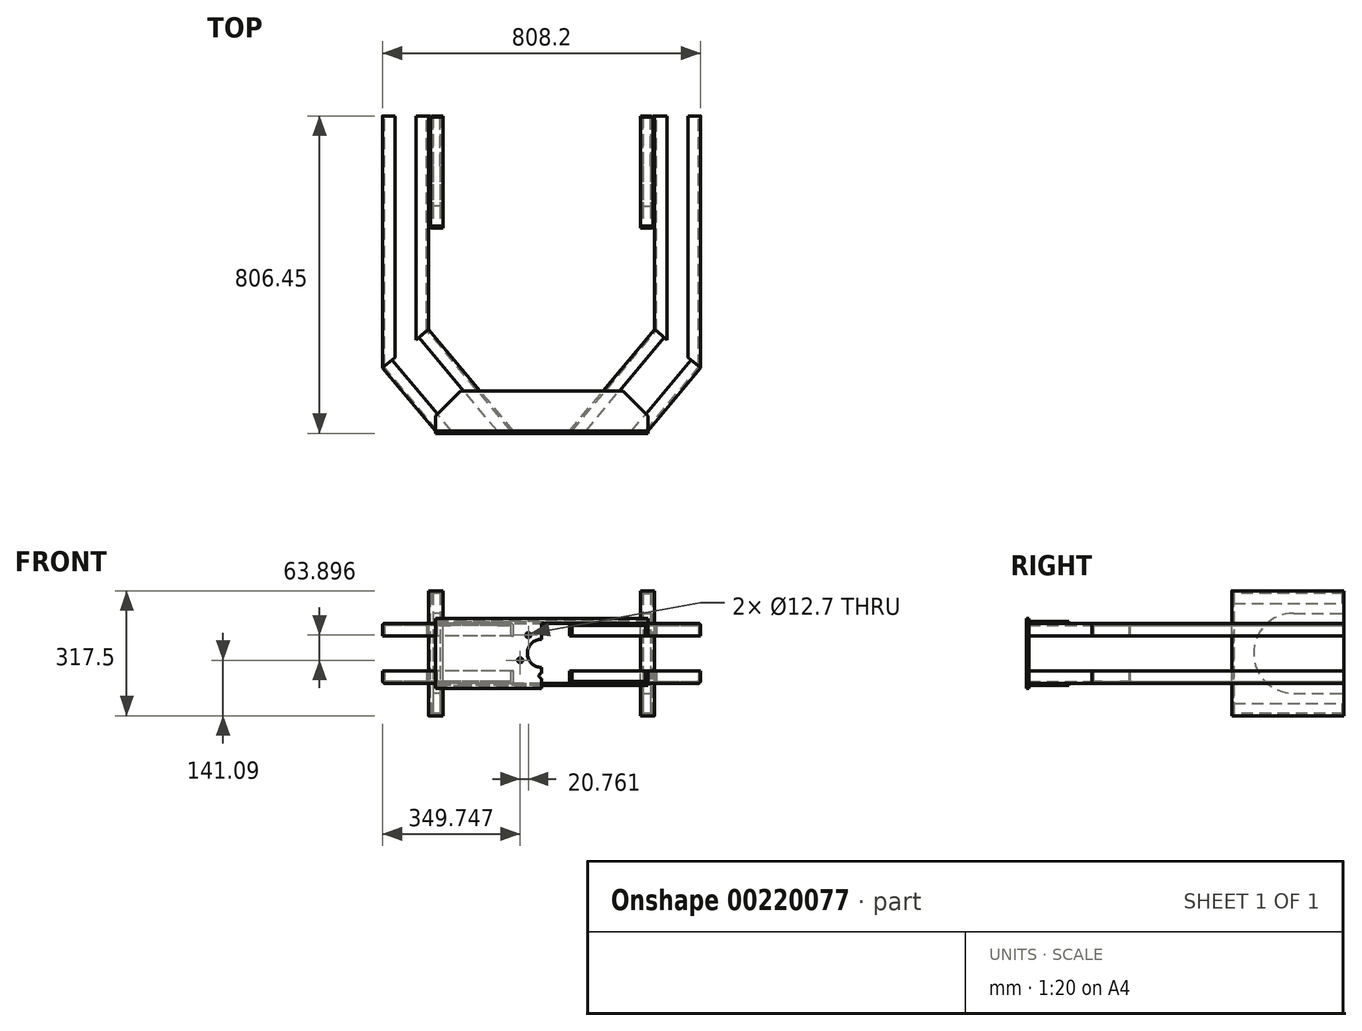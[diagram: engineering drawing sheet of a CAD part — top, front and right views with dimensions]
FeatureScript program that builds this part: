
annotation { "Feature Type Name" : "Feature", "Feature Type Description" : "" }
export const myFeature = defineFeature(function(context is Context, id is Id, definition is map)
    precondition{}
    {
        {
            var Q0;
            Q0=qCreatedBy(makeId("Right.planeOp"),FACE);
            cPlane(context, id + "F0", {"entities" : qUnion([Q0]), "cplaneType" : CPlaneType.OFFSET, "offset" : 276.22 * mm, "width" : 152.4 * mm, "height" : 152.4 * mm});
        }
        {
            var Q0;
            Q0=qCreatedBy(makeId("Front.planeOp"),FACE);
            cPlane(context, id + "F1", {"entities" : qUnion([Q0]), "cplaneType" : CPlaneType.OFFSET, "offset" : 679.45 * mm, "oppositeDirection" : true, "width" : 152.4 * mm, "height" : 152.4 * mm});
        }
        {
            var Q0;
            Q0=qCreatedBy(id+"F0.planeOp",FACE);
            var sketch = newSketch(context, id + "F2", { "sketchPlane" : qUnion([Q0])});
            skLineSegment(sketch, "E0", {"start": v(-327.65, 0) * mm, "end": v(926.93, 0) * mm, "construction": true});
            skLineSegment(sketch, "E1", {"start": v(679.45, -237.46) * mm, "end": v(679.45, 292.03) * mm, "construction": true});
            skLineSegment(sketch, "E2.bottom", {"start": v(806.45, 152.4) * mm, "end": v(527.05, 152.4) * mm});
            skLineSegment(sketch, "E2.top", {"start": v(806.45, -152.4) * mm, "end": v(527.05, -152.4) * mm});
            skLineSegment(sketch, "E2.right", {"start": v(527.05, 152.4) * mm, "end": v(527.05, -152.4) * mm});
            skPoint(sketch, "E2.middle", {"position": v(679.45, 0) * mm});
            skArc(sketch, "E3", {"start": v(679.45, 101.6) * mm, "mid": v(577.85, 0) * mm, "end": v(679.45, -101.6) * mm});
            skLineSegment(sketch, "E4", {"start": v(679.45, 101.6) * mm, "end": v(806.45, 101.6) * mm});
            skLineSegment(sketch, "E5", {"start": v(679.45, -101.6) * mm, "end": v(806.45, -101.6) * mm});
            skLineSegment(sketch, "E6", {"start": v(806.45, 152.4) * mm, "end": v(806.45, 101.6) * mm});
            skPoint(sketch, "E2.left.start.orphan", {"position": v(831.85, 152.4) * mm});
            skLineSegment(sketch, "E7.trimOffspring", {"start": v(806.45, -101.6) * mm, "end": v(806.45, -152.4) * mm});
            skPoint(sketch, "E8.orphan", {"position": v(831.85, -152.4) * mm});
            skSolve(sketch);
        }
        {
            var Q0;
            Q0=qSketchRegion(id+"F2",true);
            extrude(context, id + "F3", {"entities" : qUnion([Q0]), "oppositeDirection" : true, "depth" : 18.29 * mm});
        }
        {
            var Q0;
            Q0=makeQuery(id+"F3.opExtrude","SWEPT_BODY",BODY,{"disambiguationData":[OSD([sQuery(id+"F2.wireOp",EDGE,"E2.bottom"),sQuery(id+"F2.wireOp",EDGE,"E2.top"),sQuery(id+"F2.wireOp",EDGE,"E2.right"),sQuery(id+"F2.wireOp",EDGE,"E3"),sQuery(id+"F2.wireOp",EDGE,"E4"),sQuery(id+"F2.wireOp",EDGE,"E5"),sQuery(id+"F2.wireOp",EDGE,"E6"),sQuery(id+"F2.wireOp",EDGE,"E7.trimOffspring")])]});
            var Q1;
            Q1=qCreatedBy(makeId("Right.planeOp"),FACE);
            mirror(context, id + "F4", {"entities" : qUnion([Q0]), "mirrorPlane" : qUnion([Q1])});
        }
        {
            var Q0;
            Q0=qCreatedBy(makeId("Front.planeOp"),FACE);
            var sketch = newSketch(context, id + "F5", { "sketchPlane" : qUnion([Q0])});
            skLineSegment(sketch, "E9.bottom", {"start": v(269.88, 88.9) * mm, "end": v(-269.88, 88.9) * mm});
            skLineSegment(sketch, "E9.top", {"start": v(269.88, -88.9) * mm, "end": v(-269.88, -88.9) * mm});
            skLineSegment(sketch, "E9.left", {"start": v(269.88, 88.9) * mm, "end": v(269.88, -88.9) * mm});
            skLineSegment(sketch, "E9.right", {"start": v(-269.88, 88.9) * mm, "end": v(-269.88, -88.9) * mm});
            skPoint(sketch, "E9.middle", {"position": v(0, 0) * mm});
            skCircle(sketch, "E10", {"center": v(0, 0) * mm, "radius": 35.79 * mm});
            skCircle(sketch, "E11", {"center": v(0, 0) * mm, "radius": 57.15 * mm, "construction": true});
            skLineSegment(sketch, "E12", {"start": v(0, 0) * mm, "end": v(0, 133.78) * mm, "construction": true});
            skCircle(sketch, "E13", {"center": v(0, 0) * mm, "radius": 76.68 * mm, "construction": true});
            skLineSegment(sketch, "E14", {"start": v(0, 0) * mm, "end": v(0, -130.52) * mm, "construction": true});
            skCircle(sketch, "E15", {"center": v(0, -57.15) * mm, "radius": 6.35 * mm});
            skCircle(sketch, "E16.1.0", {"center": v(54.35, -17.66) * mm, "radius": 6.35 * mm});
            skCircle(sketch, "E16.2.0", {"center": v(33.6, 46.24) * mm, "radius": 6.35 * mm});
            skCircle(sketch, "E16.3.0", {"center": v(-33.6, 46.24) * mm, "radius": 6.35 * mm});
            skCircle(sketch, "E16.4.0", {"center": v(-54.35, -17.66) * mm, "radius": 6.35 * mm});
            skSolve(sketch);
        }
        {
            var Q0;
            Q0=qSketchRegion(id+"F5",true);
            extrude(context, id + "F6", {"entities" : qUnion([Q0]), "oppositeDirection" : true, "depth" : 6.35 * mm});
        }
        {
            var Q0;
            Q0=makeQuery(id+"F3.opExtrude","SWEPT_FACE",FACE,{"disambiguationData":[OSD([sQuery(id+"F2.wireOp",EDGE,"E6")])]});
            var sketch = newSketch(context, id + "F7", { "sketchPlane" : qUnion([Q0])});
            skLineSegment(sketch, "E17.0", {"start": v(-276.23, 152.4) * mm, "end": v(-276.23, 127) * mm});
            skLineSegment(sketch, "E18", {"start": v(-282.58, 158.75) * mm, "end": v(-282.58, 127) * mm});
            skLineSegment(sketch, "E19.0", {"start": v(-276.23, -127) * mm, "end": v(-276.23, -152.4) * mm});
            skLineSegment(sketch, "E20", {"start": v(-282.58, -127) * mm, "end": v(-282.58, -158.75) * mm});
            skLineSegment(sketch, "E21", {"start": v(-282.58, -158.75) * mm, "end": v(-250.83, -158.75) * mm});
            skLineSegment(sketch, "E22", {"start": v(-282.58, -127) * mm, "end": v(-276.23, -127) * mm});
            skLineSegment(sketch, "E23", {"start": v(-250.83, -152.4) * mm, "end": v(-250.83, -158.75) * mm});
            skPoint(sketch, "E24.0.start.orphan", {"position": v(-276.23, -101.6) * mm});
            skLineSegment(sketch, "E25", {"start": v(-276.23, -152.4) * mm, "end": v(-250.83, -152.4) * mm});
            skLineSegment(sketch, "E26", {"start": v(-282.58, 127) * mm, "end": v(-276.23, 127) * mm});
            skLineSegment(sketch, "E27", {"start": v(-250.83, 158.75) * mm, "end": v(-250.83, 152.4) * mm});
            skLineSegment(sketch, "E28", {"start": v(-276.23, 152.4) * mm, "end": v(-250.83, 152.4) * mm});
            skLineSegment(sketch, "E29", {"start": v(-282.58, 158.75) * mm, "end": v(-250.83, 158.75) * mm});
            skSolve(sketch);
        }
        {
            var Q0;
            Q0=qSketchRegion(id+"F7",true);
            var Q1;
            Q1=makeQuery(id+"F3.opExtrude","SWEPT_FACE",FACE,{"disambiguationData":[OSD([sQuery(id+"F2.wireOp",EDGE,"E2.right")])]});
            extrude(context, id + "F8", {"entities" : qUnion([Q0]), "endBound" : BoundingType.UP_TO_SURFACE, "oppositeDirection" : true, "endBoundEntityFace" : qUnion([Q1]), "depth" : 25.4 * mm});
        }
        {
            var Q0;
            Q0=makeQuery(id+"F8.opExtrude","SWEPT_EDGE",EDGE,{"disambiguationData":[OSD([sQuery(id+"F7.wireOp",EDGE,"E19.0"),sQuery(id+"F7.wireOp",EDGE,"E25")])]});
            var Q1;
            Q1=makeQuery(id+"F8.opExtrude","SWEPT_EDGE",EDGE,{"disambiguationData":[OSD([sQuery(id+"F7.wireOp",EDGE,"E17.0"),sQuery(id+"F7.wireOp",EDGE,"E28")])]});
            fillet(context, id + "F9", {"entities" : qUnion([Q0, Q1]), "radius" : 2.3 * mm, "tangentPropagation" : true, "allowEdgeOverflow" : false});
        }
        {
            var Q0;
            Q0=makeQuery(id+"F8.opExtrude","SWEPT_EDGE",EDGE,{"disambiguationData":[OSD([sQuery(id+"F7.wireOp",EDGE,"E18"),sQuery(id+"F7.wireOp",EDGE,"E29")])]});
            var Q1;
            Q1=makeQuery(id+"F8.opExtrude","SWEPT_EDGE",EDGE,{"disambiguationData":[OSD([sQuery(id+"F7.wireOp",EDGE,"E20"),sQuery(id+"F7.wireOp",EDGE,"E21")])]});
            fillet(context, id + "F10", {"entities" : qUnion([Q0, Q1]), "radius" : 8.64 * mm, "tangentPropagation" : true, "allowEdgeOverflow" : false});
        }
        {
            var Q0;
            Q0=makeQuery(id+"F8.opExtrude","TWEAK_EDGE",EDGE,{"derivedFrom":[makeQuery(id+"F3.opExtrude","SWEPT_FACE",FACE,{"disambiguationData":[OSD([sQuery(id+"F2.wireOp",EDGE,"E2.right")])]}),makeQuery(id+"F7.imprint","IMPRINT",EDGE,{"derivedFrom":sQuery(id+"F7.wireOp",EDGE,"E29")})]});
            var Q1;
            Q1=makeQuery(id+"F8.opExtrude","CAP_EDGE",EDGE,{"disambiguationData":[OSD([sQuery(id+"F7.wireOp",EDGE,"E29")])],"isStart":true});
            var Q2;
            Q2=makeQuery(id+"F8.opExtrude","TWEAK_EDGE",EDGE,{"derivedFrom":[makeQuery(id+"F3.opExtrude","SWEPT_FACE",FACE,{"disambiguationData":[OSD([sQuery(id+"F2.wireOp",EDGE,"E2.right")])]}),makeQuery(id+"F7.imprint","IMPRINT",EDGE,{"derivedFrom":sQuery(id+"F7.wireOp",EDGE,"E21")})]});
            var Q3;
            Q3=makeQuery(id+"F8.opExtrude","CAP_EDGE",EDGE,{"disambiguationData":[OSD([sQuery(id+"F7.wireOp",EDGE,"E20")])],"isStart":true});
            chamfer(context, id + "F11", {"entities" : qUnion([Q0, Q1, Q2, Q3]), "width" : 3.17 * mm, "tangentPropagation" : true});
        }
        {
            var Q0;
            Q0=makeQuery(id+"F8.opExtrude","SWEPT_FACE",FACE,{"disambiguationData":[OSD([sQuery(id+"F7.wireOp",EDGE,"E29")])]});
            var sketch = newSketch(context, id + "F12", { "sketchPlane" : qUnion([Q0])});
            skLineSegment(sketch, "E30.0", {"start": v(282.58, 806.45) * mm, "end": v(282.58, 529.34) * mm});
            skLineSegment(sketch, "E31", {"start": v(287.35, 806.45) * mm, "end": v(287.35, 529.34) * mm});
            skLineSegment(sketch, "E32", {"start": v(250.83, 522.27) * mm, "end": v(280.29, 522.27) * mm});
            skPoint(sketch, "E33.visualSharp", {"position": v(282.58, 527.05) * mm});
            skArc(sketch, "E33.filletArc", {"start": v(280.29, 527.05) * mm, "mid": v(281.9, 527.72) * mm, "end": v(282.58, 529.34) * mm});
            skArc(sketch, "E34.filletArc", {"start": v(280.29, 522.27) * mm, "mid": v(285.28, 524.34) * mm, "end": v(287.35, 529.34) * mm});
            skLineSegment(sketch, "E35.0", {"start": v(280.29, 527.05) * mm, "end": v(250.83, 527.05) * mm});
            skLineSegment(sketch, "E36", {"start": v(250.83, 527.05) * mm, "end": v(250.83, 522.27) * mm});
            skLineSegment(sketch, "E37.0.3", {"start": v(282.58, 806.45) * mm, "end": v(287.35, 806.45) * mm});
            skSolve(sketch);
        }
        {
            var Q0;
            Q0=qSketchRegion(id+"F12",true);
            var Q1;
            Q1=makeQuery(id+"F8.opExtrude","SWEPT_FACE",FACE,{"disambiguationData":[OSD([sQuery(id+"F7.wireOp",EDGE,"E21")])]});
            extrude(context, id + "F13", {"entities" : qUnion([Q0]), "oppositeDirection" : true, "endBoundEntityFace" : qUnion([Q1]), "depth" : 317.5 * mm});
        }
        {
            var Q0;
            Q0=makeQuery(id+"F8.opExtrude","SWEPT_BODY",BODY,{"disambiguationData":[OSD([sQuery(id+"F7.wireOp",EDGE,"E17.0"),sQuery(id+"F7.wireOp",EDGE,"E18"),sQuery(id+"F7.wireOp",EDGE,"E26"),sQuery(id+"F7.wireOp",EDGE,"E27"),sQuery(id+"F7.wireOp",EDGE,"E28"),sQuery(id+"F7.wireOp",EDGE,"E29")])]});
            var Q1;
            Q1=makeQuery(id+"F8.opExtrude","SWEPT_BODY",BODY,{"disambiguationData":[OSD([sQuery(id+"F7.wireOp",EDGE,"E19.0"),sQuery(id+"F7.wireOp",EDGE,"E20"),sQuery(id+"F7.wireOp",EDGE,"E21"),sQuery(id+"F7.wireOp",EDGE,"E22"),sQuery(id+"F7.wireOp",EDGE,"E23"),sQuery(id+"F7.wireOp",EDGE,"E25")])]});
            var Q2;
            Q2=makeQuery(id+"F13.opExtrude","SWEPT_BODY",BODY,{"disambiguationData":[OSD([sQuery(id+"F12.wireOp",EDGE,"E30.0"),sQuery(id+"F12.wireOp",EDGE,"bLRiQibS-mOqF-sB3g-dTbY-Dugds5DFzCdw"),sQuery(id+"F12.wireOp",EDGE,"4U48pxRf-2JOl-YEqJ-IsQ4-tJ9NNKT0FoYB"),sQuery(id+"F12.wireOp",EDGE,"E31"),sQuery(id+"F12.wireOp",EDGE,"2b993bdc-ece1-4cef-9b09-9722fc915676.filletArc"),sQuery(id+"F12.wireOp",EDGE,"7b43bb2a-2bf7-418a-ae6b-22cfb534edce.filletArc"),sQuery(id+"F12.wireOp",EDGE,"k2mm9kqk-ofhh-FyIz-BeeO-gpMZ8WsVDZ71"),sQuery(id+"F12.wireOp",EDGE,"E32"),sQuery(id+"F12.wireOp",EDGE,"E33.filletArc"),sQuery(id+"F12.wireOp",EDGE,"E34.filletArc"),sQuery(id+"F12.wireOp",EDGE,"E35.0"),sQuery(id+"F12.wireOp",EDGE,"E36")])]});
            var Q3;
            Q3=qCreatedBy(makeId("Right.planeOp"),FACE);
            mirror(context, id + "F14", {"entities" : qUnion([Q0, Q1, Q2]), "mirrorPlane" : qUnion([Q3])});
        }
        {
            var Q0;
            Q0=qCreatedBy(makeId("Top.planeOp"),FACE);
            cPlane(context, id + "F15", {"entities" : qUnion([Q0]), "cplaneType" : CPlaneType.OFFSET, "offset" : 76.2 * mm, "width" : 152.4 * mm, "height" : 152.4 * mm});
        }
        {
            var Q0;
            Q0=qCreatedBy(id+"F15.planeOp",FACE);
            var sketch = newSketch(context, id + "F16", { "sketchPlane" : qUnion([Q0])});
            skLineSegment(sketch, "E38.0", {"start": v(269.88, 6.35) * mm, "end": v(-269.88, 6.35) * mm});
            skLineSegment(sketch, "E39", {"start": v(-269.88, 107.95) * mm, "end": v(269.88, 107.95) * mm});
            skLineSegment(sketch, "E40", {"start": v(269.88, 6.35) * mm, "end": v(269.88, 107.95) * mm});
            skLineSegment(sketch, "E41", {"start": v(-269.88, 6.35) * mm, "end": v(-269.88, 107.95) * mm});
            skSolve(sketch);
        }
        {
            var Q0;
            Q0=qSketchRegion(id+"F16",true);
            extrude(context, id + "F17", {"entities" : qUnion([Q0]), "depth" : 4.78 * mm});
        }
        {
            var Q0;
            Q0=qCreatedBy(makeId("Top.planeOp"),FACE);
            cPlane(context, id + "F18", {"entities" : qUnion([Q0]), "cplaneType" : CPlaneType.OFFSET, "offset" : 76.2 * mm, "oppositeDirection" : true, "width" : 152.4 * mm, "height" : 152.4 * mm});
        }
        {
            var Q0;
            Q0=qCreatedBy(id+"F18.planeOp",FACE);
            var sketch = newSketch(context, id + "F19", { "sketchPlane" : qUnion([Q0])});
            skLineSegment(sketch, "E42.0", {"start": v(269.88, 6.35) * mm, "end": v(-269.88, 6.35) * mm});
            skLineSegment(sketch, "E43", {"start": v(-269.88, 107.95) * mm, "end": v(269.88, 107.95) * mm});
            skLineSegment(sketch, "E44", {"start": v(269.88, 107.95) * mm, "end": v(269.88, 6.35) * mm});
            skLineSegment(sketch, "E45", {"start": v(-269.88, 107.95) * mm, "end": v(-269.88, 6.35) * mm});
            skSolve(sketch);
        }
        {
            var Q0;
            Q0=qSketchRegion(id+"F19",true);
            extrude(context, id + "F20", {"entities" : qUnion([Q0]), "oppositeDirection" : true, "depth" : 4.78 * mm});
        }
        {
            var Q0;
            Q0=makeQuery(id+"F17.opExtrude","SWEPT_EDGE",EDGE,{"disambiguationData":[OSD([sQuery(id+"F16.wireOp",EDGE,"E39"),sQuery(id+"F16.wireOp",EDGE,"E40")])]});
            var Q1;
            Q1=makeQuery(id+"F17.opExtrude","SWEPT_EDGE",EDGE,{"disambiguationData":[OSD([sQuery(id+"F16.wireOp",EDGE,"E39"),sQuery(id+"F16.wireOp",EDGE,"E41")])]});
            var Q2;
            Q2=makeQuery(id+"F20.opExtrude","SWEPT_EDGE",EDGE,{"disambiguationData":[OSD([sQuery(id+"F19.wireOp",EDGE,"E43"),sQuery(id+"F19.wireOp",EDGE,"E45")])]});
            var Q3;
            Q3=makeQuery(id+"F20.opExtrude","SWEPT_EDGE",EDGE,{"disambiguationData":[OSD([sQuery(id+"F19.wireOp",EDGE,"E43"),sQuery(id+"F19.wireOp",EDGE,"E44")])]});
            chamfer(context, id + "F21", {"entities" : qUnion([Q0, Q1, Q2, Q3]), "width" : 63.5 * mm, "tangentPropagation" : true});
        }
        {
            var Q0;
            Q0=qCreatedBy(id+"F15.planeOp",FACE);
            var sketch = newSketch(context, id + "F22", { "sketchPlane" : qUnion([Q0])});
            skLineSegment(sketch, "E46.0", {"start": v(287.35, 264.26) * mm, "end": v(287.35, 806.45) * mm});
            skLineSegment(sketch, "E47.0", {"start": v(88.9, 6.35) * mm, "end": v(287.35, 204.8) * mm, "construction": true});
            skLineSegment(sketch, "E48.0", {"start": v(269.88, 6.35) * mm, "end": v(70.94, 6.35) * mm});
            skPoint(sketch, "E49.orphan", {"position": v(269.88, 6.35) * mm});
            skPoint(sketch, "E50.orphan", {"position": v(287.35, 204.8) * mm});
            skPoint(sketch, "E51.orphan", {"position": v(-269.88, 6.35) * mm});
            skLineSegment(sketch, "E52", {"start": v(70.94, 6.35) * mm, "end": v(287.35, 264.26) * mm});
            skLineSegment(sketch, "E53", {"start": v(287.35, 264.26) * mm, "end": v(404.1, 166.3) * mm});
            skLineSegment(sketch, "E54", {"start": v(269.88, 6.35) * mm, "end": v(404.1, 166.3) * mm});
            skLineSegment(sketch, "E55", {"start": v(404.1, 166.3) * mm, "end": v(404.1, 806.45) * mm});
            skLineSegment(sketch, "E56.trimOffspring", {"start": v(287.35, 806.45) * mm, "end": v(404.1, 806.45) * mm});
            skSolve(sketch);
        }
        {
            var Q0;
            Q0=qCreatedBy(makeId("Front.planeOp"),FACE);
            cPlane(context, id + "F23", {"entities" : qUnion([Q0]), "cplaneType" : CPlaneType.OFFSET, "offset" : 806.45 * mm, "oppositeDirection" : true, "width" : 152.4 * mm, "height" : 152.4 * mm});
        }
        {
            var Q0;
            Q0=qCreatedBy(id+"F23.planeOp",FACE);
            var sketch = newSketch(context, id + "F24", { "sketchPlane" : qUnion([Q0])});
            skArc(sketch, "E57.0", {"start": v(287.35, -69.14) * mm, "mid": v(289.42, -74.13) * mm, "end": v(294.41, -76.2) * mm});
            skArc(sketch, "E58.0", {"start": v(292.13, -69.14) * mm, "mid": v(292.8, -70.76) * mm, "end": v(294.41, -71.42) * mm});
            skArc(sketch, "E59.0", {"start": v(294.41, 76.2) * mm, "mid": v(289.42, 74.13) * mm, "end": v(287.35, 69.14) * mm});
            skArc(sketch, "E60.0", {"start": v(294.41, 71.42) * mm, "mid": v(292.8, 70.76) * mm, "end": v(292.13, 69.14) * mm});
            skLineSegment(sketch, "E61", {"start": v(294.41, 71.42) * mm, "end": v(319.1, 71.42) * mm});
            skLineSegment(sketch, "E62", {"start": v(294.41, 76.2) * mm, "end": v(319.1, 76.2) * mm});
            skLineSegment(sketch, "E63", {"start": v(287.35, 69.14) * mm, "end": v(287.35, 44.45) * mm});
            skLineSegment(sketch, "E64", {"start": v(292.13, 69.14) * mm, "end": v(292.13, 44.45) * mm});
            skLineSegment(sketch, "E65", {"start": v(319.1, 76.2) * mm, "end": v(319.1, 71.42) * mm});
            skLineSegment(sketch, "E66", {"start": v(294.41, -71.42) * mm, "end": v(319.1, -71.42) * mm});
            skLineSegment(sketch, "E67", {"start": v(294.41, -76.2) * mm, "end": v(319.1, -76.2) * mm});
            skLineSegment(sketch, "E68", {"start": v(319.1, -71.42) * mm, "end": v(319.1, -76.2) * mm});
            skLineSegment(sketch, "E69", {"start": v(292.13, -44.45) * mm, "end": v(287.35, -44.45) * mm});
            skLineSegment(sketch, "E70", {"start": v(292.13, 44.45) * mm, "end": v(287.35, 44.45) * mm});
            skLineSegment(sketch, "E71.trimOffspring", {"start": v(287.35, -44.45) * mm, "end": v(287.35, -69.14) * mm});
            skLineSegment(sketch, "E72.trimOffspring", {"start": v(292.13, -44.45) * mm, "end": v(292.13, -69.14) * mm});
            skSolve(sketch);
        }
        {
            var Q0;
            Q0 = qSketchRegion(id + "F24", true);
            extrude(context, id + "F25", {"entities" : qUnion([Q0]), "depth" : 571.5 * mm});
        }
        {
            var Q0;
            Q0=qCreatedBy(id+"F23.planeOp",FACE);
            var sketch = newSketch(context, id + "F26", { "sketchPlane" : qUnion([Q0])});
            skLineSegment(sketch, "E73", {"start": v(404.09, 69.14) * mm, "end": v(404.09, 44.45) * mm});
            skLineSegment(sketch, "E74", {"start": v(372.34, 76.2) * mm, "end": v(397.03, 76.2) * mm});
            skLineSegment(sketch, "E75", {"start": v(372.34, 71.42) * mm, "end": v(397.03, 71.42) * mm});
            skLineSegment(sketch, "E76", {"start": v(372.34, -71.42) * mm, "end": v(397.03, -71.42) * mm});
            skLineSegment(sketch, "E77", {"start": v(372.34, -76.2) * mm, "end": v(397.03, -76.2) * mm});
            skLineSegment(sketch, "E78", {"start": v(399.31, 69.14) * mm, "end": v(399.31, 44.45) * mm});
            skLineSegment(sketch, "E79", {"start": v(404.09, 44.45) * mm, "end": v(399.31, 44.45) * mm});
            skLineSegment(sketch, "E80", {"start": v(404.09, -44.45) * mm, "end": v(399.31, -44.45) * mm});
            skLineSegment(sketch, "E81", {"start": v(372.34, -71.42) * mm, "end": v(372.34, -76.2) * mm});
            skLineSegment(sketch, "E82", {"start": v(372.34, 76.2) * mm, "end": v(372.34, 71.42) * mm});
            skLineSegment(sketch, "E83.trimOffspring", {"start": v(399.31, -44.45) * mm, "end": v(399.31, -69.14) * mm});
            skLineSegment(sketch, "E84.trimOffspring", {"start": v(404.09, -44.45) * mm, "end": v(404.09, -69.14) * mm});
            skArc(sketch, "E85.filletArc", {"start": v(397.03, -71.42) * mm, "mid": v(398.64, -70.76) * mm, "end": v(399.31, -69.14) * mm});
            skArc(sketch, "E86.filletArc", {"start": v(399.31, 69.14) * mm, "mid": v(398.64, 70.76) * mm, "end": v(397.03, 71.42) * mm});
            skArc(sketch, "E87.filletArc", {"start": v(404.09, 69.14) * mm, "mid": v(402.02, 74.13) * mm, "end": v(397.03, 76.2) * mm});
            skArc(sketch, "E88.filletArc", {"start": v(397.03, -76.2) * mm, "mid": v(402.02, -74.13) * mm, "end": v(404.09, -69.14) * mm});
            skSolve(sketch);
        }
        {
            var Q0;
            Q0 = qSketchRegion(id + "F26", true);
            extrude(context, id + "F27", {"entities" : qUnion([Q0]), "depth" : 641.35 * mm});
        }
        {
            var Q0;
            Q0=qCreatedBy(id+"F15.planeOp",FACE);
            var sketch = newSketch(context, id + "F28", { "sketchPlane" : qUnion([Q0])});
            skLineSegment(sketch, "E89.0", {"start": v(287.35, 264.26) * mm, "end": v(426.06, 147.86) * mm});
            skLineSegment(sketch, "E90", {"start": v(287.35, 264.26) * mm, "end": v(230.04, 195.95) * mm});
            skLineSegment(sketch, "E91", {"start": v(230.04, 195.95) * mm, "end": v(368.75, 79.56) * mm});
            skLineSegment(sketch, "E92", {"start": v(368.75, 79.56) * mm, "end": v(426.06, 147.86) * mm});
            skPoint(sketch, "E93.start.orphan", {"position": v(404.1, 166.3) * mm});
            skSolve(sketch);
        }
        {
            var Q0;
            Q0 = qSketchRegion(id + "F28", true);
            extrude(context, id + "F29", {"entities" : qUnion([Q0]), "operationType" : NewBodyOperationType.REMOVE, "oppositeDirection" : true, "depth" : 152.4 * mm});
        }
        {
            var Q0;
            Q0=makeQuery(id+"F29.boolean.opBoolean","COPY",FACE,{"disambiguationData":[TD([makeQuery(id+"F25.opExtrude","SWEPT_FACE",FACE,{"disambiguationData":[OSD([sQuery(id+"F24.wireOp",EDGE,"E59.0")])]})])],"derivedFrom":makeQuery(id+"F29.opExtrude","SWEPT_FACE",FACE,{"disambiguationData":[OSD([sQuery(id+"F28.wireOp",EDGE,"E89.0")])]})});
            cPlane(context, id + "F30", {"entities" : qUnion([Q0]), "cplaneType" : CPlaneType.OFFSET, "offset" : 0 * mm, "width" : 152.4 * mm, "height" : 152.4 * mm});
        }
        {
            var Q0;
            Q0=qCreatedBy(id+"F30.planeOp",FACE);
            var sketch = newSketch(context, id + "F31", { "sketchPlane" : qUnion([Q0])});
            skLineSegment(sketch, "E94.0", {"start": v(57.32, 76.2) * mm, "end": v(82.01, 76.2) * mm});
            skLineSegment(sketch, "E95.0", {"start": v(57.32, -76.2) * mm, "end": v(82.01, -76.2) * mm});
            skLineSegment(sketch, "E96", {"start": v(202.66, 69.14) * mm, "end": v(202.66, 44.45) * mm});
            skLineSegment(sketch, "E97", {"start": v(50.26, 69.14) * mm, "end": v(50.26, 44.45) * mm});
            skLineSegment(sketch, "E98", {"start": v(55.04, 69.14) * mm, "end": v(55.04, 44.45) * mm});
            skLineSegment(sketch, "E99", {"start": v(197.89, 69.14) * mm, "end": v(197.89, 44.45) * mm});
            skLineSegment(sketch, "E100", {"start": v(57.32, 71.42) * mm, "end": v(82.01, 71.42) * mm});
            skLineSegment(sketch, "E101", {"start": v(57.32, -71.42) * mm, "end": v(82.01, -71.42) * mm});
            skLineSegment(sketch, "E102", {"start": v(170.91, 76.2) * mm, "end": v(170.91, 71.42) * mm});
            skLineSegment(sketch, "E103", {"start": v(82.01, 76.2) * mm, "end": v(82.01, 71.42) * mm});
            skLineSegment(sketch, "E104", {"start": v(50.26, -44.45) * mm, "end": v(55.04, -44.45) * mm});
            skLineSegment(sketch, "E105", {"start": v(50.26, 44.45) * mm, "end": v(55.04, 44.45) * mm});
            skLineSegment(sketch, "E106.trimOffspring", {"start": v(82.01, -71.42) * mm, "end": v(82.01, -76.2) * mm});
            skLineSegment(sketch, "E107.trimOffspring", {"start": v(197.89, 44.45) * mm, "end": v(202.66, 44.45) * mm});
            skLineSegment(sketch, "E108.trimOffspring", {"start": v(170.91, -71.42) * mm, "end": v(170.91, -76.2) * mm});
            skLineSegment(sketch, "E109.trimOffspring", {"start": v(197.89, -44.45) * mm, "end": v(202.66, -44.45) * mm});
            skLineSegment(sketch, "E110.trimOffspring", {"start": v(55.04, -44.45) * mm, "end": v(55.04, -69.14) * mm});
            skLineSegment(sketch, "E111.trimOffspring", {"start": v(50.26, -44.45) * mm, "end": v(50.26, -69.14) * mm});
            skLineSegment(sketch, "E112.trimOffspring", {"start": v(170.91, -71.42) * mm, "end": v(195.6, -71.42) * mm});
            skLineSegment(sketch, "E113.trimOffspring", {"start": v(170.91, -76.2) * mm, "end": v(195.6, -76.2) * mm});
            skLineSegment(sketch, "E114.trimOffspring", {"start": v(202.66, -44.45) * mm, "end": v(202.66, -69.14) * mm});
            skLineSegment(sketch, "E115.trimOffspring", {"start": v(197.89, -44.45) * mm, "end": v(197.89, -69.14) * mm});
            skLineSegment(sketch, "E116.trimOffspring", {"start": v(170.91, 76.2) * mm, "end": v(195.6, 76.2) * mm});
            skLineSegment(sketch, "E117.trimOffspring", {"start": v(170.91, 71.42) * mm, "end": v(195.6, 71.42) * mm});
            skPoint(sketch, "E118.visualSharp", {"position": v(55.04, 71.42) * mm});
            skArc(sketch, "E118.filletArc", {"start": v(57.32, 71.42) * mm, "mid": v(55.7, 70.76) * mm, "end": v(55.04, 69.14) * mm});
            skPoint(sketch, "E119.visualSharp", {"position": v(197.89, 71.42) * mm});
            skArc(sketch, "E119.filletArc", {"start": v(197.89, 69.14) * mm, "mid": v(197.22, 70.76) * mm, "end": v(195.6, 71.42) * mm});
            skArc(sketch, "E120.filletArc", {"start": v(195.6, -71.42) * mm, "mid": v(197.22, -70.76) * mm, "end": v(197.89, -69.14) * mm});
            skArc(sketch, "E121.filletArc", {"start": v(55.04, -69.14) * mm, "mid": v(55.7, -70.76) * mm, "end": v(57.32, -71.42) * mm});
            skArc(sketch, "E122.filletArc", {"start": v(50.26, -69.14) * mm, "mid": v(52.33, -74.13) * mm, "end": v(57.32, -76.2) * mm});
            skArc(sketch, "E123.filletArc", {"start": v(195.6, -76.2) * mm, "mid": v(200.6, -74.13) * mm, "end": v(202.66, -69.14) * mm});
            skPoint(sketch, "E124.visualSharp", {"position": v(202.66, 76.2) * mm});
            skArc(sketch, "E124.filletArc", {"start": v(202.66, 69.14) * mm, "mid": v(200.6, 74.13) * mm, "end": v(195.6, 76.2) * mm});
            skPoint(sketch, "E125.visualSharp", {"position": v(50.26, 76.2) * mm});
            skArc(sketch, "E125.filletArc", {"start": v(57.32, 76.2) * mm, "mid": v(52.33, 74.13) * mm, "end": v(50.26, 69.14) * mm});
            skSolve(sketch);
        }
        {
            var Q0;
            Q0 = qSketchRegion(id + "F31", true);
            extrude(context, id + "F32", {"entities" : qUnion([Q0]), "depth" : 342.9 * mm});
        }
        {
            var Q0;
            Q0=makeQuery(id+"F32.opExtrude","SWEPT_FACE",FACE,{"disambiguationData":[OSD([sQuery(id+"F31.wireOp",EDGE,"E116.trimOffspring")])]});
            var sketch = newSketch(context, id + "F33", { "sketchPlane" : qUnion([Q0])});
            skLineSegment(sketch, "E126.0", {"start": v(299.74, 6.35) * mm, "end": v(-269.88, 6.35) * mm});
            skPoint(sketch, "E127.orphan", {"position": v(269.88, 6.35) * mm});
            skLineSegment(sketch, "E128", {"start": v(299.74, 6.35) * mm, "end": v(299.74, -137.12) * mm});
            skLineSegment(sketch, "E129", {"start": v(299.74, -137.12) * mm, "end": v(0, -137.12) * mm});
            skLineSegment(sketch, "E130", {"start": v(0, 6.35) * mm, "end": v(0, -137.12) * mm});
            skSolve(sketch);
        }
        {
            var Q0;
            Q0 = qSketchRegion(id + "F33", true);
            extrude(context, id + "F34", {"entities" : qUnion([Q0]), "operationType" : NewBodyOperationType.REMOVE, "oppositeDirection" : true, "depth" : 165.1 * mm});
        }
        {
            var Q0;
            Q0=makeQuery(id+"F27.opExtrude","SWEPT_BODY",BODY,{"disambiguationData":[OSD([sQuery(id+"F26.wireOp",EDGE,"E76"),sQuery(id+"F26.wireOp",EDGE,"E77"),sQuery(id+"F26.wireOp",EDGE,"E80"),sQuery(id+"F26.wireOp",EDGE,"E81"),sQuery(id+"F26.wireOp",EDGE,"E83.trimOffspring"),sQuery(id+"F26.wireOp",EDGE,"E84.trimOffspring"),sQuery(id+"F26.wireOp",EDGE,"E85.filletArc"),sQuery(id+"F26.wireOp",EDGE,"E88.filletArc")])]});
            var Q1;
            Q1=makeQuery(id+"F25.opExtrude","SWEPT_BODY",BODY,{"disambiguationData":[OSD([sQuery(id+"F24.wireOp",EDGE,"E57.0"),sQuery(id+"F24.wireOp",EDGE,"E58.0"),sQuery(id+"F24.wireOp",EDGE,"E66"),sQuery(id+"F24.wireOp",EDGE,"E67"),sQuery(id+"F24.wireOp",EDGE,"E68"),sQuery(id+"F24.wireOp",EDGE,"E69"),sQuery(id+"F24.wireOp",EDGE,"E71.trimOffspring"),sQuery(id+"F24.wireOp",EDGE,"E72.trimOffspring")])]});
            var Q2;
            Q2=makeQuery(id+"F25.opExtrude","SWEPT_BODY",BODY,{"disambiguationData":[OSD([sQuery(id+"F24.wireOp",EDGE,"E59.0"),sQuery(id+"F24.wireOp",EDGE,"E60.0"),sQuery(id+"F24.wireOp",EDGE,"E61"),sQuery(id+"F24.wireOp",EDGE,"E62"),sQuery(id+"F24.wireOp",EDGE,"E63"),sQuery(id+"F24.wireOp",EDGE,"E64"),sQuery(id+"F24.wireOp",EDGE,"E65"),sQuery(id+"F24.wireOp",EDGE,"E70")])]});
            var Q3;
            Q3=makeQuery(id+"F27.opExtrude","SWEPT_BODY",BODY,{"disambiguationData":[OSD([sQuery(id+"F26.wireOp",EDGE,"E73"),sQuery(id+"F26.wireOp",EDGE,"E74"),sQuery(id+"F26.wireOp",EDGE,"E75"),sQuery(id+"F26.wireOp",EDGE,"E78"),sQuery(id+"F26.wireOp",EDGE,"E79"),sQuery(id+"F26.wireOp",EDGE,"E82"),sQuery(id+"F26.wireOp",EDGE,"E86.filletArc"),sQuery(id+"F26.wireOp",EDGE,"E87.filletArc")])]});
            var Q4;
            Q4=makeQuery(id+"F32.opExtrude","SWEPT_BODY",BODY,{"disambiguationData":[OSD([sQuery(id+"F31.wireOp",EDGE,"E94.0"),sQuery(id+"F31.wireOp",EDGE,"E97"),sQuery(id+"F31.wireOp",EDGE,"E98"),sQuery(id+"F31.wireOp",EDGE,"E100"),sQuery(id+"F31.wireOp",EDGE,"E103"),sQuery(id+"F31.wireOp",EDGE,"E105"),sQuery(id+"F31.wireOp",EDGE,"E118.filletArc"),sQuery(id+"F31.wireOp",EDGE,"E125.filletArc")])]});
            var Q5;
            Q5=makeQuery(id+"F32.opExtrude","SWEPT_BODY",BODY,{"disambiguationData":[OSD([sQuery(id+"F31.wireOp",EDGE,"E95.0"),sQuery(id+"F31.wireOp",EDGE,"E101"),sQuery(id+"F31.wireOp",EDGE,"E104"),sQuery(id+"F31.wireOp",EDGE,"E106.trimOffspring"),sQuery(id+"F31.wireOp",EDGE,"E110.trimOffspring"),sQuery(id+"F31.wireOp",EDGE,"E111.trimOffspring"),sQuery(id+"F31.wireOp",EDGE,"E121.filletArc"),sQuery(id+"F31.wireOp",EDGE,"E122.filletArc")])]});
            var Q6;
            Q6=makeQuery(id+"F32.opExtrude","SWEPT_BODY",BODY,{"disambiguationData":[OSD([sQuery(id+"F31.wireOp",EDGE,"E96"),sQuery(id+"F31.wireOp",EDGE,"E99"),sQuery(id+"F31.wireOp",EDGE,"E102"),sQuery(id+"F31.wireOp",EDGE,"E107.trimOffspring"),sQuery(id+"F31.wireOp",EDGE,"E116.trimOffspring"),sQuery(id+"F31.wireOp",EDGE,"E117.trimOffspring"),sQuery(id+"F31.wireOp",EDGE,"E119.filletArc"),sQuery(id+"F31.wireOp",EDGE,"E124.filletArc")])]});
            var Q7;
            Q7=makeQuery(id+"F32.opExtrude","SWEPT_BODY",BODY,{"disambiguationData":[OSD([sQuery(id+"F31.wireOp",EDGE,"E108.trimOffspring"),sQuery(id+"F31.wireOp",EDGE,"E109.trimOffspring"),sQuery(id+"F31.wireOp",EDGE,"E112.trimOffspring"),sQuery(id+"F31.wireOp",EDGE,"E113.trimOffspring"),sQuery(id+"F31.wireOp",EDGE,"E114.trimOffspring"),sQuery(id+"F31.wireOp",EDGE,"E115.trimOffspring"),sQuery(id+"F31.wireOp",EDGE,"E120.filletArc"),sQuery(id+"F31.wireOp",EDGE,"E123.filletArc")])]});
            var Q8;
            Q8=qCreatedBy(makeId("Right.planeOp"),FACE);
            mirror(context, id + "F35", {"entities" : qUnion([Q0, Q1, Q2, Q3, Q4, Q5, Q6, Q7]), "mirrorPlane" : qUnion([Q8])});
        }
    });
